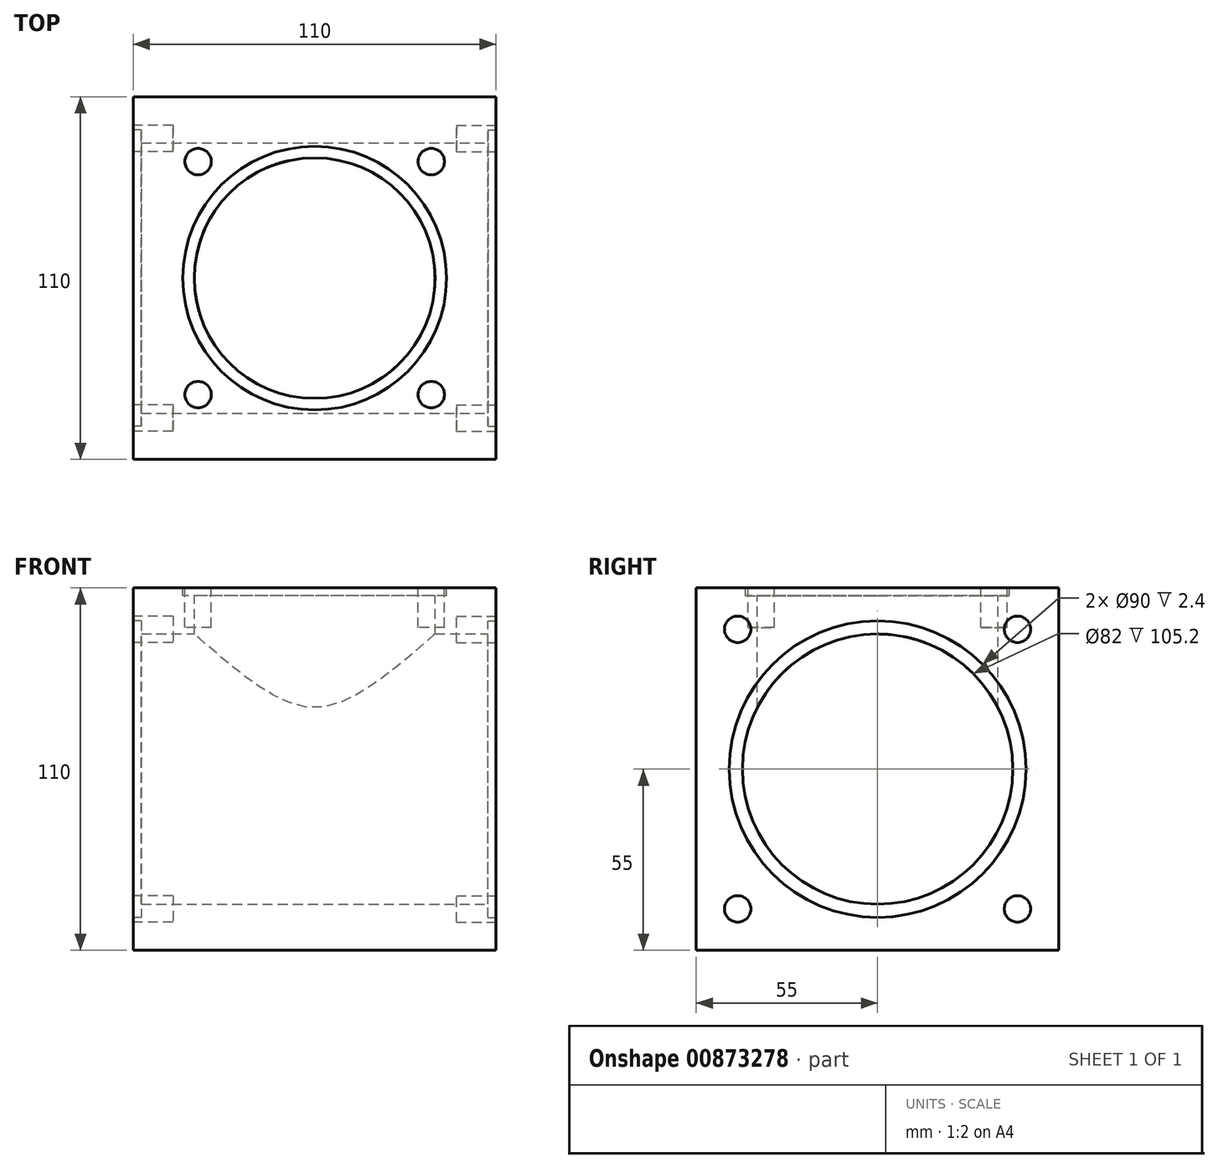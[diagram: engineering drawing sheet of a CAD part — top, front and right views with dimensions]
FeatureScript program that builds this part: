
annotation { "Feature Type Name" : "Feature", "Feature Type Description" : "" }
export const myFeature = defineFeature(function(context is Context, id is Id, definition is map)
    precondition{}
    {
        {
            var Q0;
            Q0=qCreatedBy(makeId("Top.planeOp"),FACE);
            var sketch = newSketch(context, id + "F0", { "sketchPlane" : qUnion([Q0])});
            skLineSegment(sketch, "E0.bottom", {"start": v(55, -55) * mm, "end": v(-55, -55) * mm});
            skLineSegment(sketch, "E0.top", {"start": v(55, 55) * mm, "end": v(-55, 55) * mm});
            skLineSegment(sketch, "E0.left", {"start": v(55, -55) * mm, "end": v(55, 55) * mm});
            skLineSegment(sketch, "E0.right", {"start": v(-55, -55) * mm, "end": v(-55, 55) * mm});
            skPoint(sketch, "E0.middle", {"position": v(0, 0) * mm});
            skCircle(sketch, "E1", {"center": v(0, 0) * mm, "radius": 40 * mm});
            skCircle(sketch, "E2", {"center": v(0, 0) * mm, "radius": 50 * mm, "construction": true});
            skCircle(sketch, "E3", {"center": v(0, 0) * mm, "radius": 36.5 * mm});
            skLineSegment(sketch, "E4", {"start": v(63.34, 0) * mm, "end": v(-63.34, 0) * mm, "construction": true});
            skLineSegment(sketch, "E5", {"start": v(0, 60.86) * mm, "end": v(0, -61.13) * mm, "construction": true});
            skLineSegment(sketch, "E6", {"start": v(0, 0) * mm, "end": v(65.97, 65.97) * mm, "construction": true});
            skCircle(sketch, "E7", {"center": v(35.36, 35.36) * mm, "radius": 4 * mm});
            skCircle(sketch, "E8.1.0", {"center": v(-35.36, 35.36) * mm, "radius": 4 * mm});
            skCircle(sketch, "E8.2.0", {"center": v(-35.36, -35.36) * mm, "radius": 4 * mm});
            skCircle(sketch, "E8.3.0", {"center": v(35.36, -35.36) * mm, "radius": 4 * mm});
            skSolve(sketch);
        }
        {
            var Q0;
            Q0=makeQuery(id+"F0.imprint","IMPRINT",FACE,{"disambiguationData":[TD([[makeQuery(id+"F0.imprint","IMPRINT",EDGE,{"derivedFrom":sQuery(id+"F0.wireOp",EDGE,"E0.bottom")}),-1.0]])]});
            var Q1;
            Q1=makeQuery(id+"F0.imprint","IMPRINT",FACE,{"disambiguationData":[TD([[makeQuery(id+"F0.imprint","IMPRINT",EDGE,{"derivedFrom":sQuery(id+"F0.wireOp",EDGE,"E8.3.0")}),1.0]])]});
            var Q2;
            Q2=makeQuery(id+"F0.imprint","IMPRINT",FACE,{"disambiguationData":[TD([[makeQuery(id+"F0.imprint","IMPRINT",EDGE,{"derivedFrom":sQuery(id+"F0.wireOp",EDGE,"E8.2.0")}),1.0]])]});
            var Q3;
            Q3=makeQuery(id+"F0.imprint","IMPRINT",FACE,{"disambiguationData":[TD([[makeQuery(id+"F0.imprint","IMPRINT",EDGE,{"derivedFrom":sQuery(id+"F0.wireOp",EDGE,"E3")}),1.0]])]});
            var Q4;
            Q4=makeQuery(id+"F0.imprint","IMPRINT",FACE,{"disambiguationData":[TD([[makeQuery(id+"F0.imprint","IMPRINT",EDGE,{"derivedFrom":sQuery(id+"F0.wireOp",EDGE,"E1")}),1.0]])]});
            var Q5;
            Q5=makeQuery(id+"F0.imprint","IMPRINT",FACE,{"disambiguationData":[TD([[makeQuery(id+"F0.imprint","IMPRINT",EDGE,{"derivedFrom":sQuery(id+"F0.wireOp",EDGE,"E8.1.0")}),1.0]])]});
            var Q6;
            Q6=makeQuery(id+"F0.imprint","IMPRINT",FACE,{"disambiguationData":[TD([[makeQuery(id+"F0.imprint","IMPRINT",EDGE,{"derivedFrom":sQuery(id+"F0.wireOp",EDGE,"E7")}),1.0]])]});
            extrude(context, id + "F1", {"entities" : qUnion([Q0, Q1, Q2, Q3, Q4, Q5, Q6]), "oppositeDirection" : true, "depth" : 110 * mm, "offsetDistance" : 25 * mm});
        }
        {
            var Q0;
            Q0=makeQuery(id+"F0.imprint","IMPRINT",FACE,{"disambiguationData":[TD([[makeQuery(id+"F0.imprint","IMPRINT",EDGE,{"derivedFrom":sQuery(id+"F0.wireOp",EDGE,"E1")}),1.0]])]});
            extrude(context, id + "F2", {"entities" : qUnion([Q0]), "operationType" : NewBodyOperationType.REMOVE, "oppositeDirection" : true, "depth" : 2.4 * mm, "offsetDistance" : 25 * mm});
        }
        {
            var Q0;
            Q0=makeQuery(id+"F0.imprint","IMPRINT",FACE,{"disambiguationData":[TD([[makeQuery(id+"F0.imprint","IMPRINT",EDGE,{"derivedFrom":sQuery(id+"F0.wireOp",EDGE,"E3")}),1.0]])]});
            extrude(context, id + "F3", {"entities" : qUnion([Q0]), "operationType" : NewBodyOperationType.REMOVE, "oppositeDirection" : true, "depth" : 36.5 * mm, "offsetDistance" : 25 * mm});
        }
        {
            var Q0;
            Q0=makeQuery(id+"F0.imprint","IMPRINT",FACE,{"disambiguationData":[TD([[makeQuery(id+"F0.imprint","IMPRINT",EDGE,{"derivedFrom":sQuery(id+"F0.wireOp",EDGE,"E7")}),1.0]])]});
            var Q1;
            Q1=makeQuery(id+"F0.imprint","IMPRINT",FACE,{"disambiguationData":[TD([[makeQuery(id+"F0.imprint","IMPRINT",EDGE,{"derivedFrom":sQuery(id+"F0.wireOp",EDGE,"E8.1.0")}),1.0]])]});
            var Q2;
            Q2=makeQuery(id+"F0.imprint","IMPRINT",FACE,{"disambiguationData":[TD([[makeQuery(id+"F0.imprint","IMPRINT",EDGE,{"derivedFrom":sQuery(id+"F0.wireOp",EDGE,"E8.2.0")}),1.0]])]});
            var Q3;
            Q3=makeQuery(id+"F0.imprint","IMPRINT",FACE,{"disambiguationData":[TD([[makeQuery(id+"F0.imprint","IMPRINT",EDGE,{"derivedFrom":sQuery(id+"F0.wireOp",EDGE,"E8.3.0")}),1.0]])]});
            extrude(context, id + "F4", {"entities" : qUnion([Q0, Q1, Q2, Q3]), "operationType" : NewBodyOperationType.REMOVE, "oppositeDirection" : true, "depth" : 12 * mm, "offsetDistance" : 25 * mm});
        }
        {
            var Q0;
            Q0=makeQuery(id+"F1.opExtrude","SWEPT_FACE",FACE,{"disambiguationData":[OSD([sQuery(id+"F0.wireOp",EDGE,"E0.left")])]});
            var sketch = newSketch(context, id + "F5", { "sketchPlane" : qUnion([Q0])});
            skLineSegment(sketch, "E9", {"start": v(0, 7.58) * mm, "end": v(0, -120.45) * mm, "construction": true});
            skLineSegment(sketch, "E10", {"start": v(55, -55) * mm, "end": v(-59.4, -55) * mm, "construction": true});
            skCircle(sketch, "E11", {"center": v(0, -55) * mm, "radius": 41 * mm});
            skCircle(sketch, "E12", {"center": v(0, -55) * mm, "radius": 45 * mm});
            skCircle(sketch, "E13", {"center": v(0, -55) * mm, "radius": 60 * mm, "construction": true});
            skLineSegment(sketch, "E14", {"start": v(0, -55) * mm, "end": v(55.25, -110.25) * mm, "construction": true});
            skCircle(sketch, "E15", {"center": v(42.43, -97.43) * mm, "radius": 4 * mm});
            skCircle(sketch, "E16.1.0", {"center": v(42.43, -12.57) * mm, "radius": 4 * mm});
            skCircle(sketch, "E16.2.0", {"center": v(-42.43, -12.57) * mm, "radius": 4 * mm});
            skCircle(sketch, "E17.1.3.0", {"center": v(-42.43, -97.43) * mm, "radius": 4 * mm});
            skSolve(sketch);
        }
        {
            var Q0;
            Q0=makeQuery(id+"F5.imprint","IMPRINT",FACE,{"disambiguationData":[TD([[makeQuery(id+"F5.imprint","IMPRINT",EDGE,{"derivedFrom":sQuery(id+"F5.wireOp",EDGE,"E11")}),1.0]])]});
            extrude(context, id + "F6", {"entities" : qUnion([Q0]), "operationType" : NewBodyOperationType.REMOVE, "endBound" : BoundingType.THROUGH_ALL, "oppositeDirection" : true, "depth" : 25 * mm, "offsetDistance" : 25 * mm});
        }
        {
            var Q0;
            Q0=makeQuery(id+"F5.imprint","IMPRINT",FACE,{"disambiguationData":[TD([[makeQuery(id+"F5.imprint","IMPRINT",EDGE,{"derivedFrom":sQuery(id+"F5.wireOp",EDGE,"E11")}),-1.0]])]});
            extrude(context, id + "F7", {"entities" : qUnion([Q0]), "operationType" : NewBodyOperationType.REMOVE, "oppositeDirection" : true, "depth" : 2.4 * mm, "offsetDistance" : 25 * mm});
        }
        {
            var Q0;
            Q0=makeQuery(id+"F5.imprint","IMPRINT",FACE,{"disambiguationData":[TD([[makeQuery(id+"F5.imprint","IMPRINT",EDGE,{"derivedFrom":sQuery(id+"F5.wireOp",EDGE,"E16.1.0")}),1.0]])]});
            var Q1;
            Q1=makeQuery(id+"F5.imprint","IMPRINT",FACE,{"disambiguationData":[TD([[makeQuery(id+"F5.imprint","IMPRINT",EDGE,{"derivedFrom":sQuery(id+"F5.wireOp",EDGE,"E16.2.0")}),1.0]])]});
            var Q2;
            Q2=makeQuery(id+"F5.imprint","IMPRINT",FACE,{"disambiguationData":[TD([[makeQuery(id+"F5.imprint","IMPRINT",EDGE,{"derivedFrom":sQuery(id+"F5.wireOp",EDGE,"E17.1.3.0")}),1.0]])]});
            var Q3;
            Q3=makeQuery(id+"F5.imprint","IMPRINT",FACE,{"disambiguationData":[TD([[makeQuery(id+"F5.imprint","IMPRINT",EDGE,{"derivedFrom":sQuery(id+"F5.wireOp",EDGE,"E15")}),1.0]])]});
            extrude(context, id + "F8", {"entities" : qUnion([Q0, Q1, Q2, Q3]), "operationType" : NewBodyOperationType.REMOVE, "oppositeDirection" : true, "depth" : 12 * mm, "offsetDistance" : 25 * mm});
        }
        {
            var Q0;
            Q0=makeQuery(id+"F1.opExtrude","SWEPT_FACE",FACE,{"disambiguationData":[OSD([sQuery(id+"F0.wireOp",EDGE,"E0.right")])]});
            var sketch = newSketch(context, id + "F9", { "sketchPlane" : qUnion([Q0])});
            skLineSegment(sketch, "E18", {"start": v(0, 7.14) * mm, "end": v(0, -120.88) * mm, "construction": true});
            skLineSegment(sketch, "E19", {"start": v(55, -55) * mm, "end": v(-59.4, -55) * mm, "construction": true});
            skCircle(sketch, "E20", {"center": v(0, -55) * mm, "radius": 41 * mm});
            skCircle(sketch, "E21", {"center": v(0, -55) * mm, "radius": 45 * mm});
            skCircle(sketch, "E22", {"center": v(0, -55) * mm, "radius": 60 * mm, "construction": true});
            skLineSegment(sketch, "E23", {"start": v(0, -55) * mm, "end": v(68.69, -123.69) * mm, "construction": true});
            skCircle(sketch, "E24", {"center": v(42.43, -97.43) * mm, "radius": 4 * mm});
            skCircle(sketch, "E25.1.0", {"center": v(42.43, -12.57) * mm, "radius": 4 * mm});
            skCircle(sketch, "E25.2.0", {"center": v(-42.43, -12.57) * mm, "radius": 4 * mm});
            skCircle(sketch, "E26.1.3.0", {"center": v(-42.43, -97.43) * mm, "radius": 4 * mm});
            skSolve(sketch);
        }
        {
            var Q0;
            Q0=makeQuery(id+"F9.imprint","IMPRINT",FACE,{"disambiguationData":[TD([[makeQuery(id+"F9.imprint","IMPRINT",EDGE,{"derivedFrom":sQuery(id+"F9.wireOp",EDGE,"E20")}),1.0]])]});
            extrude(context, id + "F10", {"entities" : qUnion([Q0]), "operationType" : NewBodyOperationType.REMOVE, "oppositeDirection" : true, "depth" : 2.4 * mm, "offsetDistance" : 25 * mm});
        }
        {
            var Q0;
            Q0=makeQuery(id+"F9.imprint","IMPRINT",FACE,{"disambiguationData":[TD([[makeQuery(id+"F9.imprint","IMPRINT",EDGE,{"derivedFrom":sQuery(id+"F9.wireOp",EDGE,"E25.2.0")}),1.0]])]});
            var Q1;
            Q1=makeQuery(id+"F9.imprint","IMPRINT",FACE,{"disambiguationData":[TD([[makeQuery(id+"F9.imprint","IMPRINT",EDGE,{"derivedFrom":sQuery(id+"F9.wireOp",EDGE,"E25.1.0")}),1.0]])]});
            var Q2;
            Q2=makeQuery(id+"F9.imprint","IMPRINT",FACE,{"disambiguationData":[TD([[makeQuery(id+"F9.imprint","IMPRINT",EDGE,{"derivedFrom":sQuery(id+"F9.wireOp",EDGE,"E24")}),1.0]])]});
            var Q3;
            Q3=makeQuery(id+"F9.imprint","IMPRINT",FACE,{"disambiguationData":[TD([[makeQuery(id+"F9.imprint","IMPRINT",EDGE,{"derivedFrom":sQuery(id+"F9.wireOp",EDGE,"E26.1.3.0")}),1.0]])]});
            extrude(context, id + "F11", {"entities" : qUnion([Q0, Q1, Q2, Q3]), "operationType" : NewBodyOperationType.REMOVE, "oppositeDirection" : true, "depth" : 12 * mm, "offsetDistance" : 25 * mm});
        }
    });
